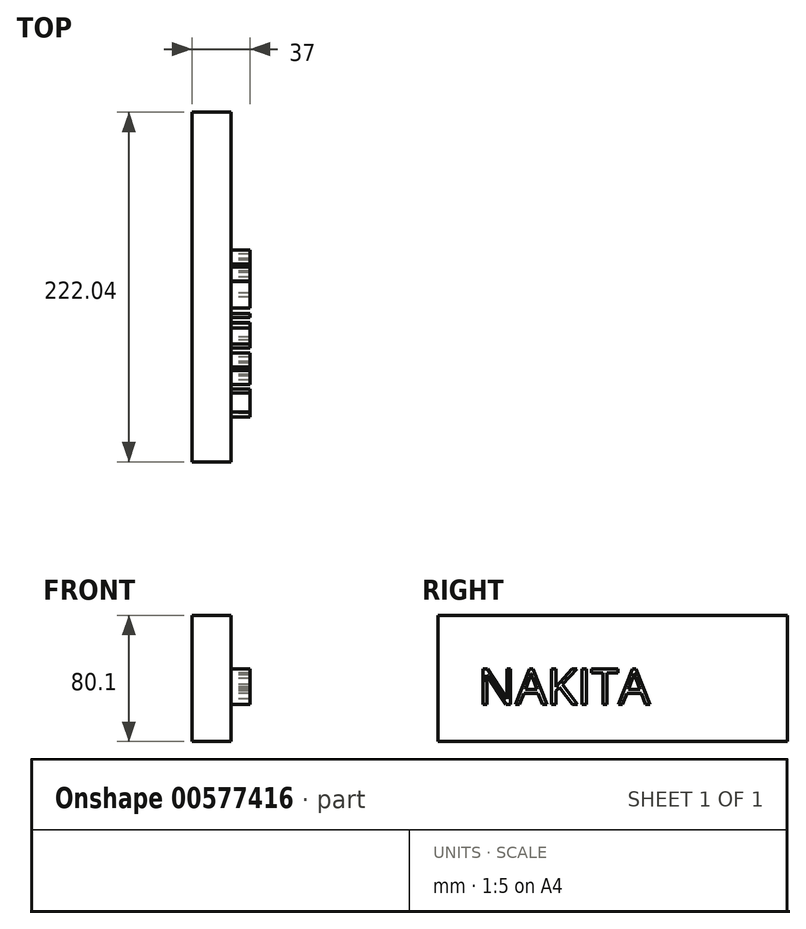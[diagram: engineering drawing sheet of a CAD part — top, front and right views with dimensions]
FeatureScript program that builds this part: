
annotation { "Feature Type Name" : "Feature", "Feature Type Description" : "" }
export const myFeature = defineFeature(function(context is Context, id is Id, definition is map)
    precondition{}
    {
        {
            var Q0;
            Q0=qCreatedBy(makeId("Right.planeOp"),FACE);
            var sketch = newSketch(context, id + "F0", { "sketchPlane" : qUnion([Q0])});
            skLineSegment(sketch, "E0.bottom", {"start": v(-111.02, 40.05) * mm, "end": v(111.02, 40.05) * mm});
            skLineSegment(sketch, "E0.top", {"start": v(-111.02, -40.05) * mm, "end": v(111.02, -40.05) * mm});
            skLineSegment(sketch, "E0.left", {"start": v(-111.02, 40.05) * mm, "end": v(-111.02, -40.05) * mm});
            skLineSegment(sketch, "E0.right", {"start": v(111.02, 40.05) * mm, "end": v(111.02, -40.05) * mm});
            skPoint(sketch, "E0.middle", {"position": v(0, 0) * mm});
            skSolve(sketch);
        }
        {
            var Q0;
            Q0=makeQuery(id+"F0.imprint","IMPRINT",FACE,{"disambiguationData":[TD([[makeQuery(id+"F0.imprint","IMPRINT",EDGE,{"derivedFrom":sQuery(id+"F0.wireOp",EDGE,"E0.bottom")}),-1.0]])]});
            extrude(context, id + "F1", {"entities" : qUnion([Q0]), "depth" : 25 * mm, "offsetDistance" : 25 * mm});
        }
        {
            var Q0;
            Q0=makeQuery(id+"F1.opExtrude","CAP_FACE",FACE,{"disambiguationData":[OSD([sQuery(id+"F0.wireOp",EDGE,"E0.bottom"),sQuery(id+"F0.wireOp",EDGE,"E0.top"),sQuery(id+"F0.wireOp",EDGE,"E0.left"),sQuery(id+"F0.wireOp",EDGE,"E0.right")])],"isStart":false});
            var sketch = newSketch(context, id + "F2", { "sketchPlane" : qUnion([Q0])});
            skText(sketch, "E1", { "text": "NAKITA\n", "fontName": "OpenSans-Regular.ttf"});
            const initialGuessF2  = {"E1": [-0.08554, -0.01665, 1, 0, 0.02267]};
            skSetInitialGuess(sketch, initialGuessF2);
            skSolve(sketch);
        }
        {
            var Q0;
            Q0 = qSketchRegion(id + "F2", true);
            extrude(context, id + "F3", {"entities" : qUnion([Q0]), "operationType" : NewBodyOperationType.ADD, "depth" : 12 * mm, "offsetDistance" : 25 * mm});
        }
    });
